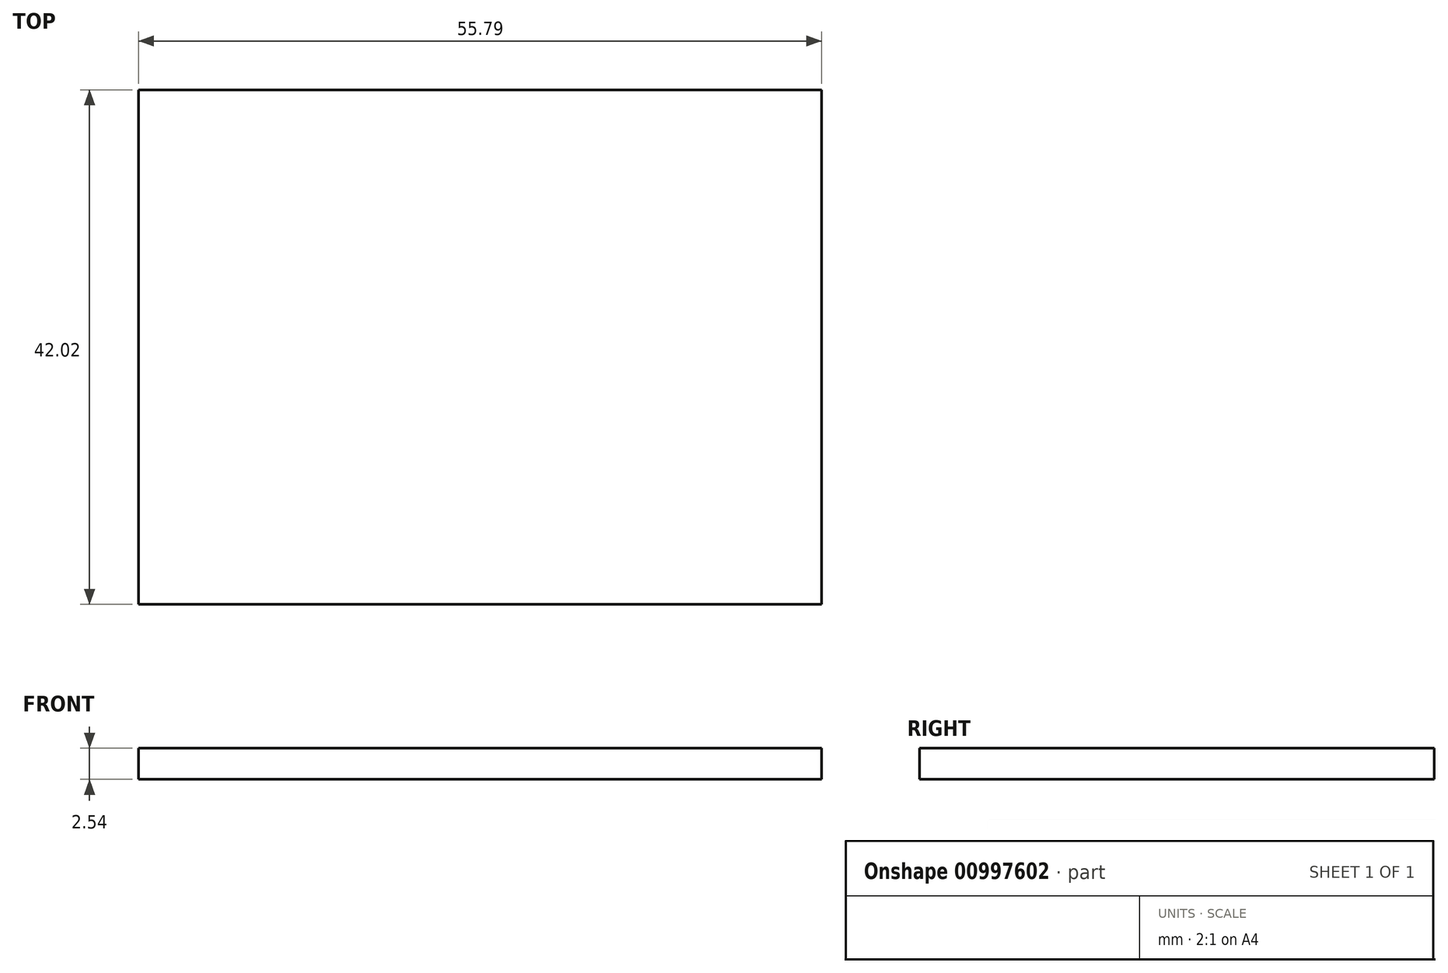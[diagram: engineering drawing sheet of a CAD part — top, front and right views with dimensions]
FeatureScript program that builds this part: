
annotation { "Feature Type Name" : "Feature", "Feature Type Description" : "" }
export const myFeature = defineFeature(function(context is Context, id is Id, definition is map)
    precondition{}
    {
        {
            var Q0;
            Q0=qCreatedBy(makeId("Top.planeOp"),FACE);
            var sketch = newSketch(context, id + "F0", { "sketchPlane" : qUnion([Q0])});
            skLineSegment(sketch, "E0.bottom", {"start": v(0, 0) * mm, "end": v(55.8, 0) * mm});
            skLineSegment(sketch, "E0.top", {"start": v(0, 42.02) * mm, "end": v(55.8, 42.02) * mm});
            skLineSegment(sketch, "E0.left", {"start": v(0, 0) * mm, "end": v(0, 42.02) * mm});
            skLineSegment(sketch, "E0.right", {"start": v(55.8, 0) * mm, "end": v(55.8, 42.02) * mm});
            skSolve(sketch);
        }
        {
            var Q0;
            Q0 = qSketchRegion(id + "F0", true);
            extrude(context, id + "F1", {"entities" : qUnion([Q0]), "depth" : 2.54 * mm, "offsetDistance" : 25.4 * mm});
        }
    });
